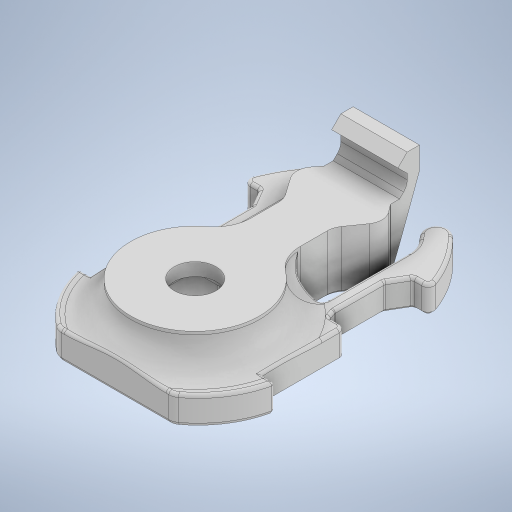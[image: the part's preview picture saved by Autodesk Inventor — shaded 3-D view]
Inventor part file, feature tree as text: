
AUTODESK INVENTOR PART (.ipt)
format: ipt  version: 2024 (Build 280153000, 153)  size: 963,072 bytes
history: native  units: in
note: dims shown in document units (in); Inventor stores cm internally (conversion verified against a paired STEP export)
features: extrude x8, chamfer x5, fillet x5, direct_edit x4, move_body x4, sketch x3, revolve x1
ambient origin geometry x8: Origin, YZ Plane, XZ Plane, XY Plane, X Axis, Y Axis, Z Axis, Center Point
bodies: Solid1 (feature_tree)
feature tree (30):
  sketch  "Sketch1"  dims[d0=0.5348in d1=0.0394in]
  extrude  "Extrusion1"  Depth=0.0394in
  extrude  "Extrusion2"  Depth=0.0197in
  sketch  "Sketch2"  dims[d2=0.0197in d3=0.0197in]
  extrude  "Extrusion3"  Depth=0.6201in
  extrude  "Extrusion4"  Depth=0.0118in
  extrude  "Extrusion5"  Depth=0.0118in
  extrude  "Extrusion6"  Depth=0.0118in
  direct_edit  "Direct Edit1"
  extrude  "Extrusion7"  Depth=0.0118in
  chamfer  "Chamfer1"  Distance=0.0787in
  direct_edit  "Direct Edit2"
  extrude  "Extrusion8"  Depth=0.0118in
  chamfer  "Chamfer2"  Distance=0.1476in
  chamfer  "Chamfer3"  Distance=0.315in
  fillet  "Fillet1"  Radius=0.126in
  direct_edit  "Direct Edit3"
  direct_edit  "Direct Edit4"
  fillet  "Fillet2"  Radius=0.1843in
  fillet  "Fillet3"  Radius=0.0831in
  fillet  "Fillet4"  Radius=0.0394in
  fillet  "Fillet5"  Radius=0.013in
  chamfer  "Chamfer4"  Distance=0.089in
  chamfer  "Chamfer5"  Distance=0.0783in
  sketch  "Sketch3"  dims[d4=0.0197in d5=0.6201in d6=0.4882in d7=1.1063in d8=1.028in d9=0.122in d10=0.0787in d11=0.0118in d12=0.1476in d13=0.315in d14=0.126in d15=0.1843in d16=0.0831in d17=0.0394in d18=0.013in d19=0.089in d20=0.0783in d21=0.1252in d23=0.1752in d24=0.962in d26=45.0deg d27=0.8465in d28=0.0661in d29=0.2031in d30=0.3016in d31=0.052in d32=0.0394in d34=0.9963in d35=0.2213in d36=0.2542in d37=0.0591in d38=0.1083in d39=0.5898in d40=0.0059in d41=0.1575in d42=0.0394in d43=0.1575in d44=0.0in d45=1.4724in d46=0.087in d47=0.0984in d48=0.0in d49=0.4862in d50=0.2677in d51=0.0in d52=0.7087in d53=0.2165in d54=0.0in d55=0.1181in d56=0.1575in d57=0.0in d58=0.0in d59=0.126in d60=0.0in d61=0.1339in d62=0.0in d63=0.1575in d64=0.0in d65=0.0in d66=0.0197in d67=1.2254in d68=0.0787in d69=0.4252in d70=0.4528in d71=0.0in d72=0.1575in d73=0.0787in d74=45.0deg d75=0.0in d76=0.0in d77=-0.1875in d78=0.1181in d79=0.0591in d80=0.0in d81=0.0591in d82=0.0787in d83=45.0deg d84=0.0492in d85=0.0787in d86=45.0deg d87=0.0787in d88=0.1718in d89=0.0in d90=0.0in d91=-0.0551in d92=0.0in d93=0.0in d94=-0.0551in d95=0.2362in d96=0.1772in d97=0.0197in d98=0.0197in d99=0.0197in d100=0.0787in d101=45.0deg d102=0.0118in d103=0.0197in d104=45.0deg]
  move_body  "Move1"
  move_body  "Move2"
  revolve  "Rotate1"  [1 undecoded]
  move_body  "Move3"
  move_body  "Move4"
note: 1 required parameter value undecoded (feature->parameter linkage not recoverable at this tier; creation-order binding heuristic only, values carry confidence <= 0.55)
